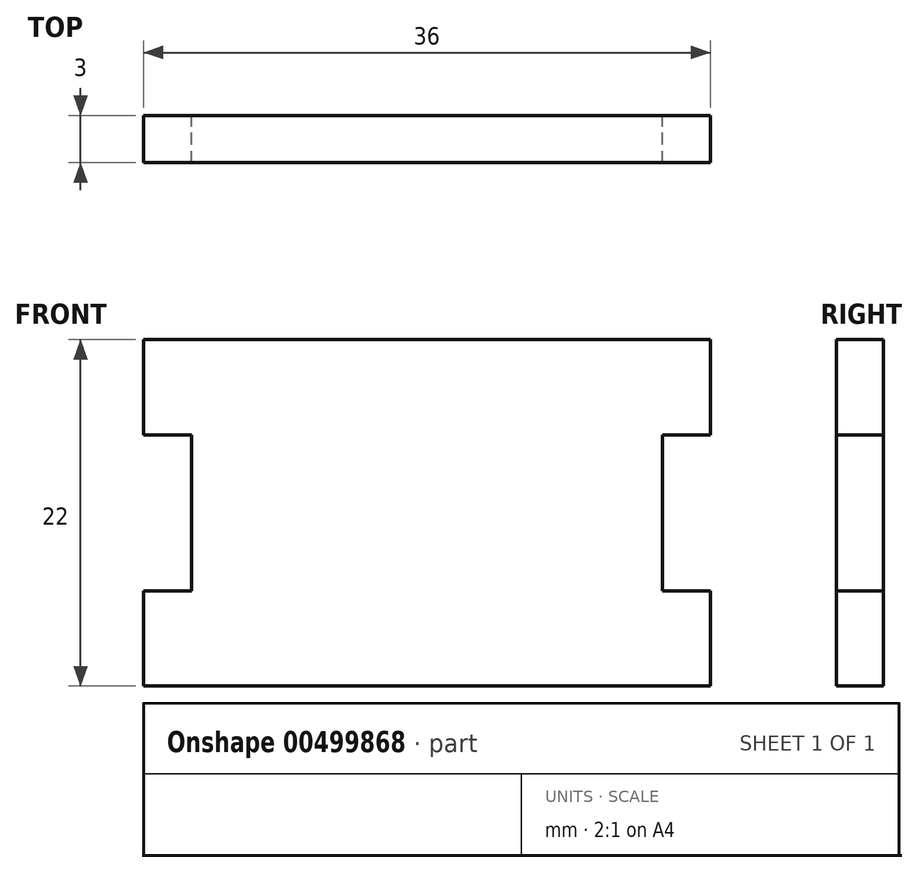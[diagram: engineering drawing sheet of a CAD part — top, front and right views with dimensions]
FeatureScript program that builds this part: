
annotation { "Feature Type Name" : "Feature", "Feature Type Description" : "" }
export const myFeature = defineFeature(function(context is Context, id is Id, definition is map)
    precondition{}
    {
        {
            var Q0;
            Q0=qCreatedBy(makeId("Front.planeOp"),FACE);
            var sketch = newSketch(context, id + "F0", { "sketchPlane" : qUnion([Q0])});
            skLineSegment(sketch, "E0.bottom", {"start": v(18, -11) * mm, "end": v(-18, -11) * mm});
            skLineSegment(sketch, "E0.top", {"start": v(18, 11) * mm, "end": v(-18, 11) * mm});
            skLineSegment(sketch, "E0.left", {"start": v(18, -11) * mm, "end": v(18, 11) * mm});
            skLineSegment(sketch, "E0.right", {"start": v(-18, -11) * mm, "end": v(-18, 11) * mm});
            skPoint(sketch, "E0.middle", {"position": v(0, 0) * mm});
            skLineSegment(sketch, "E1.bottom", {"start": v(-14.95, -4.95) * mm, "end": v(-18, -4.95) * mm});
            skLineSegment(sketch, "E1.top", {"start": v(-14.95, 4.95) * mm, "end": v(-18, 4.95) * mm});
            skLineSegment(sketch, "E1.left", {"start": v(-14.95, -4.95) * mm, "end": v(-14.95, 4.95) * mm});
            skLineSegment(sketch, "E1.right", {"start": v(-18, -4.95) * mm, "end": v(-18, 4.95) * mm});
            skPoint(sketch, "E1.middle", {"position": v(-16.47, 0) * mm});
            skLineSegment(sketch, "E2.bottom", {"start": v(18, -4.95) * mm, "end": v(14.95, -4.95) * mm});
            skLineSegment(sketch, "E2.top", {"start": v(18, 4.95) * mm, "end": v(14.95, 4.95) * mm});
            skLineSegment(sketch, "E2.left", {"start": v(18, -4.95) * mm, "end": v(18, 4.95) * mm});
            skLineSegment(sketch, "E2.right", {"start": v(14.95, -4.95) * mm, "end": v(14.95, 4.95) * mm});
            skPoint(sketch, "E2.middle", {"position": v(16.48, 0) * mm});
            skSolve(sketch);
        }
        {
            var Q0;
            {var subQ6=sQuery(id+"F0.wireOp",EDGE,"E0.bottom");Q0=makeQuery(id+"F0.imprint","IMPRINT",FACE,{"disambiguationData":[TD([[makeQuery(id+"F0.imprint","IMPRINT",EDGE,{"derivedFrom":subQ6}),-1.0]])]});}
            extrude(context, id + "F1", {"entities" : qUnion([Q0]), "depth" : 3 * mm});
        }
    });
